# Revit family: FireFighting_Fire-Reel-Box-Recessed_Galvin_381947
name_source: partatom
category: Mechanical Equipment
revit_build: Autodesk Revit MEP 2012 (Build: 20110916_2132(x64)
units: mm (PartAtom-declared; Revit-internal decimal feet)

## types (1)
- 381947
    Assembly Code = D4030
    Default Elevation = 1500 mm  [stored 4.92126 ft]
    Description = Type B Standard Fire Reel Box Recessed (Unpainted)
    DimDepth = 360 mm  [stored 1.1811 ft]
    DimHeight = 980 mm  [stored 3.21522 ft]
    DimWidth = 880 mm  [stored 2.88714 ft]
    EquipmentWeight(Kg) = 29.1
    FilterObject_ANZRS = 381947
    Instructions = http://www.galvinengineering.com.au
    Keynote = 10520
    Manufacturer = Galvin Engineering
    Material = Metal_Fire-Fighting_Stainless-Steel_15400
    Model = 381947
    ModifiedIssue_ANZRS = 20140514 $
    StyleOrType_ANZRS = Fire Fighting Equipment
    Type Comments = 381947
    URL = www.galvinengineering.com.au

note: [stored X ft] marks values corroborated as IEEE doubles in the binary element streams (Revit-internal decimal feet)

## geometry (parser evidence)
native form markers: Blend x2, Sweep x1
no freeform markers — native parametric forms only
